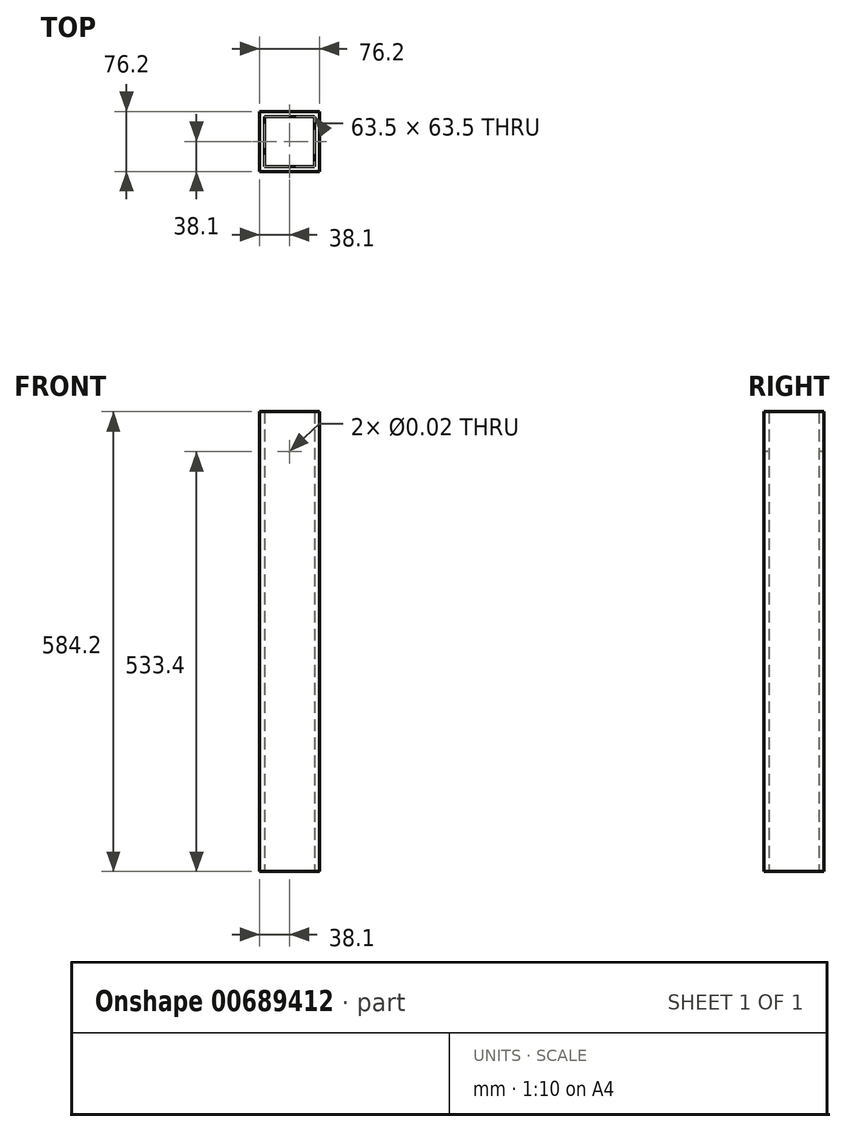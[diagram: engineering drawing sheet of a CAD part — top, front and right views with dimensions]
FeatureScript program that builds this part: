
annotation { "Feature Type Name" : "Feature", "Feature Type Description" : "" }
export const myFeature = defineFeature(function(context is Context, id is Id, definition is map)
    precondition{}
    {
        {
            var Q0;
            Q0=qCreatedBy(makeId("Top.planeOp"),FACE);
            var sketch = newSketch(context, id + "F0", { "sketchPlane" : qUnion([Q0])});
            skLineSegment(sketch, "E0.bottom", {"start": v(-38.1, 38.1) * mm, "end": v(38.1, 38.1) * mm});
            skLineSegment(sketch, "E0.top", {"start": v(-38.1, -38.1) * mm, "end": v(38.1, -38.1) * mm});
            skLineSegment(sketch, "E0.left", {"start": v(-38.1, 38.1) * mm, "end": v(-38.1, -38.1) * mm});
            skLineSegment(sketch, "E0.right", {"start": v(38.1, 38.1) * mm, "end": v(38.1, -38.1) * mm});
            skPoint(sketch, "E0.middle", {"position": v(0, 0) * mm});
            skLineSegment(sketch, "E1.bottom", {"start": v(-31.75, 31.75) * mm, "end": v(31.75, 31.75) * mm});
            skLineSegment(sketch, "E1.top", {"start": v(-31.75, -31.75) * mm, "end": v(31.75, -31.75) * mm});
            skLineSegment(sketch, "E1.left", {"start": v(-31.75, 31.75) * mm, "end": v(-31.75, -31.75) * mm});
            skLineSegment(sketch, "E1.right", {"start": v(31.75, 31.75) * mm, "end": v(31.75, -31.75) * mm});
            skSolve(sketch);
        }
        {
            var Q0;
            Q0=makeQuery(id+"F0.imprint","IMPRINT",FACE,{"disambiguationData":[TD([[makeQuery(id+"F0.imprint","IMPRINT",EDGE,{"derivedFrom":sQuery(id+"F0.wireOp",EDGE,"E0.bottom")}),-1.0]])]});
            extrude(context, id + "F1", {"entities" : qUnion([Q0]), "depth" : 584.2 * mm, "offsetDistance" : 25.4 * mm});
        }
        {
            var Q0;
            Q0=makeQuery(id+"F1.opExtrude","SWEPT_FACE",FACE,{"disambiguationData":[OSD([sQuery(id+"F0.wireOp",EDGE,"E0.top")])]});
            var sketch = newSketch(context, id + "F2", { "sketchPlane" : qUnion([Q0])});
            skPoint(sketch, "E2", {"position": v(0, 533.4) * mm});
            skSolve(sketch);
        }
        {
            var Q0;
            Q0=sQuery(id+"F2.wireOp",VERTEX,"E2");
            var Q1;
            Q1=makeQuery(id+"F1.opExtrude","SWEPT_BODY",BODY,{"disambiguationData":[OSD([sQuery(id+"F0.wireOp",EDGE,"E0.bottom"),sQuery(id+"F0.wireOp",EDGE,"E0.top"),sQuery(id+"F0.wireOp",EDGE,"E0.left"),sQuery(id+"F0.wireOp",EDGE,"E0.right"),sQuery(id+"F0.wireOp",EDGE,"E1.bottom"),sQuery(id+"F0.wireOp",EDGE,"E1.top"),sQuery(id+"F0.wireOp",EDGE,"E1.left"),sQuery(id+"F0.wireOp",EDGE,"E1.right")])]});
            hole(context, id + "F3", {"style" : HoleStyle.SIMPLE, "endStyle" : HoleEndStyle.THROUGH, "standardTappedOrClearance" : lookupTablePath({ "standard" : "ANSI", "size" : "1/2 (0.5)", "type" : "Drilled" }), "standardBlindInLast" : lookupTablePath({ "standard" : "ANSI", "size" : "1/2", "type" : "Drilled" }), "holeDiameter" : 1 / 50.8 * mm, "majorDiameter" : 6.35 * mm, "tappedDepth" : 10.3 * mm, "tapClearance" : 3, "locations" : qUnion([Q0]), "scope" : qUnion([Q1])});
        }
    });
